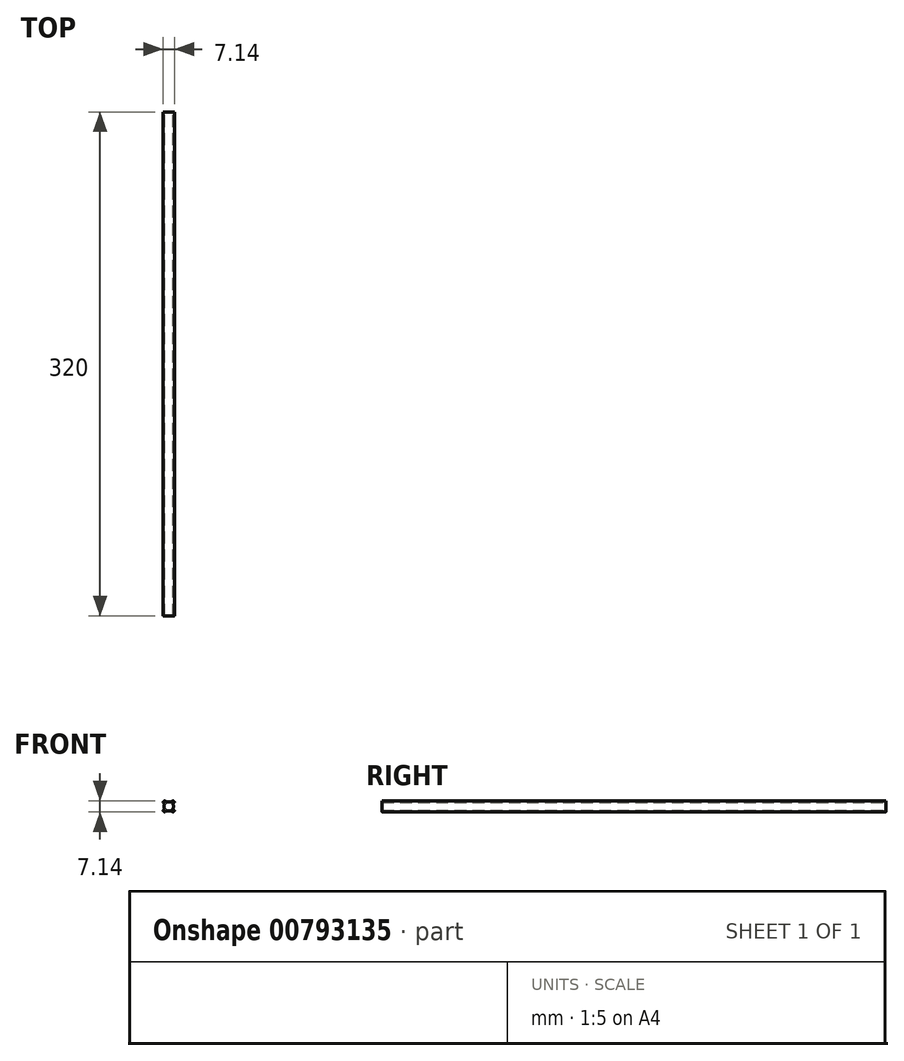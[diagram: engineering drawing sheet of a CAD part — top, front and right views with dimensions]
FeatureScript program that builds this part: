
annotation { "Feature Type Name" : "Feature", "Feature Type Description" : "" }
export const myFeature = defineFeature(function(context is Context, id is Id, definition is map)
    precondition{}
    {
        {
            var Q0;
            Q0=qCreatedBy(makeId("Front.planeOp"),FACE);
            var sketch = newSketch(context, id + "F0", { "sketchPlane" : qUnion([Q0])});
            skArc(sketch, "E0", {"start": v(-18.98, 50.3) * mm, "mid": v(-19, 50.49) * mm, "end": v(-18.92, 50.65) * mm});
            skLineSegment(sketch, "E1", {"start": v(-18.92, 50.65) * mm, "end": v(-18.18, 51.4) * mm});
            skArc(sketch, "E2", {"start": v(-18.18, 51.4) * mm, "mid": v(-18.1, 51.59) * mm, "end": v(-18.16, 51.8) * mm});
            skArc(sketch, "E3", {"start": v(-18.16, 51.8) * mm, "mid": v(-18.49, 52.15) * mm, "end": v(-18.84, 52.47) * mm});
            skArc(sketch, "E4", {"start": v(-18.84, 52.47) * mm, "mid": v(-19.05, 52.54) * mm, "end": v(-19.25, 52.45) * mm});
            skLineSegment(sketch, "E5", {"start": v(-19.25, 52.45) * mm, "end": v(-19.99, 51.71) * mm});
            skArc(sketch, "E6", {"start": v(-19.99, 51.71) * mm, "mid": v(-20.15, 51.63) * mm, "end": v(-20.33, 51.65) * mm});
            skArc(sketch, "E7", {"start": v(-20.33, 51.65) * mm, "mid": v(-21.67, 51.97) * mm, "end": v(-23, 51.65) * mm});
            skArc(sketch, "E8", {"start": v(-23, 51.65) * mm, "mid": v(-23.19, 51.63) * mm, "end": v(-23.35, 51.7) * mm});
            skLineSegment(sketch, "E9", {"start": v(-23.35, 51.7) * mm, "end": v(-24.1, 52.45) * mm});
            skArc(sketch, "E10", {"start": v(-24.1, 52.45) * mm, "mid": v(-24.29, 52.54) * mm, "end": v(-24.5, 52.47) * mm});
            skArc(sketch, "E11", {"start": v(-24.5, 52.47) * mm, "mid": v(-24.85, 52.15) * mm, "end": v(-25.17, 51.79) * mm});
            skArc(sketch, "E12", {"start": v(-25.17, 51.79) * mm, "mid": v(-25.24, 51.59) * mm, "end": v(-25.15, 51.39) * mm});
            skLineSegment(sketch, "E13", {"start": v(-25.15, 51.39) * mm, "end": v(-24.4, 50.65) * mm});
            skArc(sketch, "E14", {"start": v(-24.4, 50.65) * mm, "mid": v(-24.33, 50.49) * mm, "end": v(-24.35, 50.3) * mm});
            skArc(sketch, "E15", {"start": v(-24.35, 50.3) * mm, "mid": v(-24.67, 48.97) * mm, "end": v(-24.35, 47.63) * mm});
            skArc(sketch, "E16", {"start": v(-24.35, 47.63) * mm, "mid": v(-24.33, 47.45) * mm, "end": v(-24.4, 47.29) * mm});
            skLineSegment(sketch, "E17", {"start": v(-24.4, 47.29) * mm, "end": v(-25.15, 46.54) * mm});
            skArc(sketch, "E18", {"start": v(-25.15, 46.54) * mm, "mid": v(-25.24, 46.35) * mm, "end": v(-25.17, 46.14) * mm});
            skArc(sketch, "E19", {"start": v(-25.17, 46.14) * mm, "mid": v(-24.85, 45.79) * mm, "end": v(-24.49, 45.46) * mm});
            skArc(sketch, "E20", {"start": v(-24.49, 45.46) * mm, "mid": v(-24.29, 45.4) * mm, "end": v(-24.09, 45.48) * mm});
            skLineSegment(sketch, "E21", {"start": v(-24.09, 45.48) * mm, "end": v(-23.35, 46.22) * mm});
            skArc(sketch, "E22", {"start": v(-23.35, 46.22) * mm, "mid": v(-23.19, 46.3) * mm, "end": v(-23, 46.28) * mm});
            skArc(sketch, "E23", {"start": v(-23, 46.28) * mm, "mid": v(-21.67, 45.97) * mm, "end": v(-20.33, 46.28) * mm});
            skArc(sketch, "E24", {"start": v(-20.33, 46.28) * mm, "mid": v(-20.15, 46.3) * mm, "end": v(-19.99, 46.23) * mm});
            skLineSegment(sketch, "E25", {"start": v(-19.99, 46.23) * mm, "end": v(-19.24, 45.48) * mm});
            skArc(sketch, "E26", {"start": v(-19.24, 45.48) * mm, "mid": v(-19.05, 45.4) * mm, "end": v(-18.84, 45.46) * mm});
            skArc(sketch, "E27", {"start": v(-18.84, 45.46) * mm, "mid": v(-18.49, 45.79) * mm, "end": v(-18.16, 46.14) * mm});
            skArc(sketch, "E28", {"start": v(-18.16, 46.14) * mm, "mid": v(-18.1, 46.35) * mm, "end": v(-18.18, 46.55) * mm});
            skLineSegment(sketch, "E29", {"start": v(-18.18, 46.55) * mm, "end": v(-18.92, 47.29) * mm});
            skArc(sketch, "E30", {"start": v(-18.92, 47.29) * mm, "mid": v(-19, 47.45) * mm, "end": v(-18.98, 47.63) * mm});
            skArc(sketch, "E31", {"start": v(-18.98, 47.63) * mm, "mid": v(-18.67, 48.97) * mm, "end": v(-18.98, 50.3) * mm});
            skLineSegment(sketch, "E32", {"start": v(-21.67, 51.17) * mm, "end": v(-21.67, 46.77) * mm});
            skLineSegment(sketch, "E33", {"start": v(-19.47, 48.97) * mm, "end": v(-23.87, 48.97) * mm});
            skLineSegment(sketch, "E34", {"start": v(-19.47, 68.97) * mm, "end": v(-23.87, 68.97) * mm});
            skLineSegment(sketch, "E35", {"start": v(-21.67, 66.77) * mm, "end": v(-21.67, 71.17) * mm});
            skArc(sketch, "E36", {"start": v(-8.43, 60.55) * mm, "mid": v(-8.21, 60.72) * mm, "end": v(-8.23, 61) * mm});
            skArc(sketch, "E37", {"start": v(-8.23, 61) * mm, "mid": v(-8.84, 61.8) * mm, "end": v(-9.63, 62.41) * mm});
            skArc(sketch, "E38", {"start": v(-9.63, 62.41) * mm, "mid": v(-9.91, 62.43) * mm, "end": v(-10.08, 62.2) * mm});
            skLineSegment(sketch, "E39", {"start": v(-10.08, 62.2) * mm, "end": v(-10.22, 61.46) * mm});
            skArc(sketch, "E40", {"start": v(-10.22, 61.46) * mm, "mid": v(-10.37, 61.25) * mm, "end": v(-10.63, 61.24) * mm});
            skArc(sketch, "E41", {"start": v(-10.63, 61.24) * mm, "mid": v(-11.67, 61.47) * mm, "end": v(-12.7, 61.24) * mm});
            skArc(sketch, "E42", {"start": v(-12.7, 61.24) * mm, "mid": v(-12.96, 61.25) * mm, "end": v(-13.12, 61.46) * mm});
            skLineSegment(sketch, "E43", {"start": v(-13.12, 61.46) * mm, "end": v(-13.25, 62.2) * mm});
            skArc(sketch, "E44", {"start": v(-13.25, 62.2) * mm, "mid": v(-13.42, 62.43) * mm, "end": v(-13.7, 62.41) * mm});
            skArc(sketch, "E45", {"start": v(-13.7, 62.41) * mm, "mid": v(-14.5, 61.8) * mm, "end": v(-15.11, 61) * mm});
            skArc(sketch, "E46", {"start": v(-15.11, 61) * mm, "mid": v(-15.12, 60.72) * mm, "end": v(-14.9, 60.55) * mm});
            skLineSegment(sketch, "E47", {"start": v(-14.9, 60.55) * mm, "end": v(-14.16, 60.42) * mm});
            skArc(sketch, "E48", {"start": v(-14.16, 60.42) * mm, "mid": v(-13.95, 60.26) * mm, "end": v(-13.94, 60) * mm});
            skArc(sketch, "E49", {"start": v(-13.94, 60) * mm, "mid": v(-14.17, 58.97) * mm, "end": v(-13.94, 57.93) * mm});
            skArc(sketch, "E50", {"start": v(-13.94, 57.93) * mm, "mid": v(-13.95, 57.67) * mm, "end": v(-14.16, 57.52) * mm});
            skLineSegment(sketch, "E51", {"start": v(-14.16, 57.52) * mm, "end": v(-14.9, 57.38) * mm});
            skArc(sketch, "E52", {"start": v(-14.9, 57.38) * mm, "mid": v(-15.12, 57.21) * mm, "end": v(-15.11, 56.93) * mm});
            skArc(sketch, "E53", {"start": v(-15.11, 56.93) * mm, "mid": v(-14.5, 56.14) * mm, "end": v(-13.7, 55.53) * mm});
            skArc(sketch, "E54", {"start": v(-13.7, 55.53) * mm, "mid": v(-13.42, 55.51) * mm, "end": v(-13.25, 55.73) * mm});
            skLineSegment(sketch, "E55", {"start": v(-13.25, 55.73) * mm, "end": v(-13.12, 56.47) * mm});
            skArc(sketch, "E56", {"start": v(-13.12, 56.47) * mm, "mid": v(-12.96, 56.68) * mm, "end": v(-12.7, 56.7) * mm});
            skArc(sketch, "E57", {"start": v(-12.7, 56.7) * mm, "mid": v(-11.67, 56.47) * mm, "end": v(-10.63, 56.7) * mm});
            skArc(sketch, "E58", {"start": v(-10.63, 56.7) * mm, "mid": v(-10.37, 56.68) * mm, "end": v(-10.22, 56.47) * mm});
            skLineSegment(sketch, "E59", {"start": v(-10.22, 56.47) * mm, "end": v(-10.08, 55.73) * mm});
            skArc(sketch, "E60", {"start": v(-10.08, 55.73) * mm, "mid": v(-9.91, 55.51) * mm, "end": v(-9.63, 55.53) * mm});
            skArc(sketch, "E61", {"start": v(-9.63, 55.53) * mm, "mid": v(-8.84, 56.14) * mm, "end": v(-8.23, 56.93) * mm});
            skArc(sketch, "E62", {"start": v(-8.23, 56.93) * mm, "mid": v(-8.21, 57.21) * mm, "end": v(-8.43, 57.38) * mm});
            skLineSegment(sketch, "E63", {"start": v(-8.43, 57.38) * mm, "end": v(-9.17, 57.52) * mm});
            skArc(sketch, "E64", {"start": v(-9.17, 57.52) * mm, "mid": v(-9.38, 57.67) * mm, "end": v(-9.4, 57.93) * mm});
            skArc(sketch, "E65", {"start": v(-9.4, 57.93) * mm, "mid": v(-9.17, 58.97) * mm, "end": v(-9.4, 60) * mm});
            skArc(sketch, "E66", {"start": v(-9.4, 60) * mm, "mid": v(-9.38, 60.26) * mm, "end": v(-9.17, 60.42) * mm});
            skLineSegment(sketch, "E67", {"start": v(-9.17, 60.42) * mm, "end": v(-8.43, 60.55) * mm});
            skArc(sketch, "E68", {"start": v(-18.98, 67.63) * mm, "mid": v(-19, 67.45) * mm, "end": v(-18.93, 67.29) * mm});
            skLineSegment(sketch, "E69", {"start": v(-18.93, 67.29) * mm, "end": v(-18.19, 66.55) * mm});
            skArc(sketch, "E70", {"start": v(-18.19, 66.55) * mm, "mid": v(-18.1, 66.35) * mm, "end": v(-18.16, 66.15) * mm});
            skArc(sketch, "E71", {"start": v(-18.16, 66.15) * mm, "mid": v(-18.49, 65.79) * mm, "end": v(-18.85, 65.46) * mm});
            skArc(sketch, "E72", {"start": v(-18.85, 65.46) * mm, "mid": v(-19.05, 65.4) * mm, "end": v(-19.25, 65.49) * mm});
            skLineSegment(sketch, "E73", {"start": v(-19.25, 65.49) * mm, "end": v(-19.99, 66.23) * mm});
            skArc(sketch, "E74", {"start": v(-19.99, 66.23) * mm, "mid": v(-20.15, 66.3) * mm, "end": v(-20.33, 66.28) * mm});
            skArc(sketch, "E75", {"start": v(-20.33, 66.28) * mm, "mid": v(-21.67, 65.97) * mm, "end": v(-23, 66.28) * mm});
            skArc(sketch, "E76", {"start": v(-23, 66.28) * mm, "mid": v(-23.19, 66.3) * mm, "end": v(-23.35, 66.23) * mm});
            skLineSegment(sketch, "E77", {"start": v(-23.35, 66.23) * mm, "end": v(-24.1, 65.49) * mm});
            skArc(sketch, "E78", {"start": v(-24.1, 65.49) * mm, "mid": v(-24.29, 65.4) * mm, "end": v(-24.5, 65.46) * mm});
            skArc(sketch, "E79", {"start": v(-24.5, 65.46) * mm, "mid": v(-24.85, 65.79) * mm, "end": v(-25.17, 66.15) * mm});
            skArc(sketch, "E80", {"start": v(-25.17, 66.15) * mm, "mid": v(-25.24, 66.35) * mm, "end": v(-25.15, 66.55) * mm});
            skLineSegment(sketch, "E81", {"start": v(-25.15, 66.55) * mm, "end": v(-24.41, 67.29) * mm});
            skArc(sketch, "E82", {"start": v(-24.41, 67.29) * mm, "mid": v(-24.33, 67.45) * mm, "end": v(-24.35, 67.63) * mm});
            skArc(sketch, "E83", {"start": v(-24.35, 67.63) * mm, "mid": v(-24.67, 68.97) * mm, "end": v(-24.35, 70.3) * mm});
            skArc(sketch, "E84", {"start": v(-24.35, 70.3) * mm, "mid": v(-24.33, 70.49) * mm, "end": v(-24.41, 70.65) * mm});
            skLineSegment(sketch, "E85", {"start": v(-24.41, 70.65) * mm, "end": v(-25.15, 71.4) * mm});
            skArc(sketch, "E86", {"start": v(-25.15, 71.4) * mm, "mid": v(-25.24, 71.59) * mm, "end": v(-25.17, 71.8) * mm});
            skArc(sketch, "E87", {"start": v(-25.17, 71.8) * mm, "mid": v(-24.85, 72.15) * mm, "end": v(-24.5, 72.47) * mm});
            skArc(sketch, "E88", {"start": v(-24.5, 72.47) * mm, "mid": v(-24.29, 72.54) * mm, "end": v(-24.1, 72.45) * mm});
            skLineSegment(sketch, "E89", {"start": v(-24.1, 72.45) * mm, "end": v(-23.35, 71.71) * mm});
            skArc(sketch, "E90", {"start": v(-23.35, 71.71) * mm, "mid": v(-23.19, 71.63) * mm, "end": v(-23, 71.65) * mm});
            skArc(sketch, "E91", {"start": v(-23, 71.65) * mm, "mid": v(-21.67, 71.97) * mm, "end": v(-20.33, 71.65) * mm});
            skArc(sketch, "E92", {"start": v(-20.33, 71.65) * mm, "mid": v(-20.15, 71.63) * mm, "end": v(-19.99, 71.71) * mm});
            skLineSegment(sketch, "E93", {"start": v(-19.99, 71.71) * mm, "end": v(-19.25, 72.45) * mm});
            skArc(sketch, "E94", {"start": v(-19.25, 72.45) * mm, "mid": v(-19.05, 72.54) * mm, "end": v(-18.85, 72.47) * mm});
            skArc(sketch, "E95", {"start": v(-18.85, 72.47) * mm, "mid": v(-18.49, 72.15) * mm, "end": v(-18.16, 71.8) * mm});
            skArc(sketch, "E96", {"start": v(-18.16, 71.8) * mm, "mid": v(-18.1, 71.59) * mm, "end": v(-18.19, 71.4) * mm});
            skLineSegment(sketch, "E97", {"start": v(-18.19, 71.4) * mm, "end": v(-18.93, 70.65) * mm});
            skArc(sketch, "E98", {"start": v(-18.93, 70.65) * mm, "mid": v(-19, 70.49) * mm, "end": v(-18.98, 70.3) * mm});
            skArc(sketch, "E99", {"start": v(-18.98, 70.3) * mm, "mid": v(-18.67, 68.97) * mm, "end": v(-18.98, 67.63) * mm});
            skLineSegment(sketch, "E100", {"start": v(-6.66, 58.97) * mm, "end": v(-6.16, 58.97) * mm});
            skArc(sketch, "E101", {"start": v(21.57, 60.55) * mm, "mid": v(21.79, 60.72) * mm, "end": v(21.77, 61) * mm});
            skArc(sketch, "E102", {"start": v(21.77, 61) * mm, "mid": v(21.16, 61.8) * mm, "end": v(20.37, 62.41) * mm});
            skArc(sketch, "E103", {"start": v(20.37, 62.41) * mm, "mid": v(20.09, 62.43) * mm, "end": v(19.92, 62.2) * mm});
            skLineSegment(sketch, "E104", {"start": v(19.92, 62.2) * mm, "end": v(19.78, 61.46) * mm});
            skArc(sketch, "E105", {"start": v(19.78, 61.46) * mm, "mid": v(19.63, 61.25) * mm, "end": v(19.37, 61.24) * mm});
            skArc(sketch, "E106", {"start": v(19.37, 61.24) * mm, "mid": v(18.33, 61.47) * mm, "end": v(17.3, 61.24) * mm});
            skArc(sketch, "E107", {"start": v(17.3, 61.24) * mm, "mid": v(17.04, 61.25) * mm, "end": v(16.88, 61.46) * mm});
            skLineSegment(sketch, "E108", {"start": v(16.88, 61.46) * mm, "end": v(16.75, 62.2) * mm});
            skArc(sketch, "E109", {"start": v(16.75, 62.2) * mm, "mid": v(16.58, 62.43) * mm, "end": v(16.3, 62.41) * mm});
            skArc(sketch, "E110", {"start": v(16.3, 62.41) * mm, "mid": v(15.5, 61.8) * mm, "end": v(14.89, 61) * mm});
            skArc(sketch, "E111", {"start": v(14.89, 61) * mm, "mid": v(14.88, 60.72) * mm, "end": v(15.1, 60.55) * mm});
            skLineSegment(sketch, "E112", {"start": v(15.1, 60.55) * mm, "end": v(15.84, 60.42) * mm});
            skArc(sketch, "E113", {"start": v(15.84, 60.42) * mm, "mid": v(16.05, 60.26) * mm, "end": v(16.06, 60) * mm});
            skArc(sketch, "E114", {"start": v(16.06, 60) * mm, "mid": v(15.83, 58.97) * mm, "end": v(16.06, 57.93) * mm});
            skArc(sketch, "E115", {"start": v(16.06, 57.93) * mm, "mid": v(16.05, 57.67) * mm, "end": v(15.84, 57.52) * mm});
            skLineSegment(sketch, "E116", {"start": v(15.84, 57.52) * mm, "end": v(15.1, 57.38) * mm});
            skArc(sketch, "E117", {"start": v(15.1, 57.38) * mm, "mid": v(14.88, 57.21) * mm, "end": v(14.89, 56.93) * mm});
            skArc(sketch, "E118", {"start": v(14.89, 56.93) * mm, "mid": v(15.5, 56.14) * mm, "end": v(16.3, 55.53) * mm});
            skArc(sketch, "E119", {"start": v(16.3, 55.53) * mm, "mid": v(16.58, 55.51) * mm, "end": v(16.75, 55.73) * mm});
            skLineSegment(sketch, "E120", {"start": v(16.75, 55.73) * mm, "end": v(16.88, 56.47) * mm});
            skArc(sketch, "E121", {"start": v(16.88, 56.47) * mm, "mid": v(17.04, 56.68) * mm, "end": v(17.3, 56.7) * mm});
            skArc(sketch, "E122", {"start": v(17.3, 56.7) * mm, "mid": v(18.33, 56.47) * mm, "end": v(19.37, 56.7) * mm});
            skArc(sketch, "E123", {"start": v(19.37, 56.7) * mm, "mid": v(19.63, 56.68) * mm, "end": v(19.78, 56.47) * mm});
            skLineSegment(sketch, "E124", {"start": v(19.78, 56.47) * mm, "end": v(19.92, 55.73) * mm});
            skArc(sketch, "E125", {"start": v(19.92, 55.73) * mm, "mid": v(20.09, 55.51) * mm, "end": v(20.37, 55.53) * mm});
            skArc(sketch, "E126", {"start": v(20.37, 55.53) * mm, "mid": v(21.16, 56.14) * mm, "end": v(21.77, 56.93) * mm});
            skArc(sketch, "E127", {"start": v(21.77, 56.93) * mm, "mid": v(21.79, 57.21) * mm, "end": v(21.57, 57.38) * mm});
            skLineSegment(sketch, "E128", {"start": v(21.57, 57.38) * mm, "end": v(20.83, 57.52) * mm});
            skArc(sketch, "E129", {"start": v(20.83, 57.52) * mm, "mid": v(20.62, 57.67) * mm, "end": v(20.6, 57.93) * mm});
            skArc(sketch, "E130", {"start": v(20.6, 57.93) * mm, "mid": v(20.83, 58.97) * mm, "end": v(20.6, 60) * mm});
            skArc(sketch, "E131", {"start": v(20.6, 60) * mm, "mid": v(20.62, 60.26) * mm, "end": v(20.83, 60.42) * mm});
            skLineSegment(sketch, "E132", {"start": v(20.83, 60.42) * mm, "end": v(21.57, 60.55) * mm});
            skArc(sketch, "E133", {"start": v(25.64, 50.3) * mm, "mid": v(25.67, 50.49) * mm, "end": v(25.59, 50.65) * mm});
            skLineSegment(sketch, "E134", {"start": v(25.59, 50.65) * mm, "end": v(24.85, 51.4) * mm});
            skArc(sketch, "E135", {"start": v(24.85, 51.4) * mm, "mid": v(24.76, 51.59) * mm, "end": v(24.82, 51.8) * mm});
            skArc(sketch, "E136", {"start": v(24.82, 51.8) * mm, "mid": v(25.15, 52.15) * mm, "end": v(25.5, 52.47) * mm});
            skArc(sketch, "E137", {"start": v(25.5, 52.47) * mm, "mid": v(25.71, 52.54) * mm, "end": v(25.9, 52.45) * mm});
            skLineSegment(sketch, "E138", {"start": v(25.9, 52.45) * mm, "end": v(26.65, 51.71) * mm});
            skArc(sketch, "E139", {"start": v(26.65, 51.71) * mm, "mid": v(26.81, 51.63) * mm, "end": v(27, 51.65) * mm});
            skArc(sketch, "E140", {"start": v(27, 51.65) * mm, "mid": v(28.33, 51.97) * mm, "end": v(29.67, 51.65) * mm});
            skArc(sketch, "E141", {"start": v(29.67, 51.65) * mm, "mid": v(29.85, 51.63) * mm, "end": v(30.01, 51.7) * mm});
            skLineSegment(sketch, "E142", {"start": v(30.01, 51.7) * mm, "end": v(30.75, 52.45) * mm});
            skArc(sketch, "E143", {"start": v(30.75, 52.45) * mm, "mid": v(30.95, 52.54) * mm, "end": v(31.15, 52.47) * mm});
            skArc(sketch, "E144", {"start": v(31.15, 52.47) * mm, "mid": v(31.51, 52.15) * mm, "end": v(31.83, 51.79) * mm});
            skArc(sketch, "E145", {"start": v(31.83, 51.79) * mm, "mid": v(31.9, 51.59) * mm, "end": v(31.81, 51.39) * mm});
            skLineSegment(sketch, "E146", {"start": v(31.81, 51.39) * mm, "end": v(31.07, 50.65) * mm});
            skArc(sketch, "E147", {"start": v(31.07, 50.65) * mm, "mid": v(30.99, 50.49) * mm, "end": v(31.01, 50.3) * mm});
            skArc(sketch, "E148", {"start": v(31.01, 50.3) * mm, "mid": v(31.33, 48.97) * mm, "end": v(31.01, 47.63) * mm});
            skArc(sketch, "E149", {"start": v(31.01, 47.63) * mm, "mid": v(30.99, 47.45) * mm, "end": v(31.07, 47.29) * mm});
            skLineSegment(sketch, "E150", {"start": v(31.07, 47.29) * mm, "end": v(31.81, 46.54) * mm});
            skArc(sketch, "E151", {"start": v(31.81, 46.54) * mm, "mid": v(31.9, 46.35) * mm, "end": v(31.83, 46.14) * mm});
            skArc(sketch, "E152", {"start": v(31.83, 46.14) * mm, "mid": v(31.51, 45.79) * mm, "end": v(31.15, 45.46) * mm});
            skArc(sketch, "E153", {"start": v(31.15, 45.46) * mm, "mid": v(30.95, 45.4) * mm, "end": v(30.75, 45.48) * mm});
            skLineSegment(sketch, "E154", {"start": v(30.75, 45.48) * mm, "end": v(30.01, 46.22) * mm});
            skArc(sketch, "E155", {"start": v(30.01, 46.22) * mm, "mid": v(29.85, 46.3) * mm, "end": v(29.66, 46.28) * mm});
            skArc(sketch, "E156", {"start": v(29.66, 46.28) * mm, "mid": v(28.33, 45.97) * mm, "end": v(27, 46.28) * mm});
            skArc(sketch, "E157", {"start": v(27, 46.28) * mm, "mid": v(26.81, 46.3) * mm, "end": v(26.65, 46.23) * mm});
            skLineSegment(sketch, "E158", {"start": v(26.65, 46.23) * mm, "end": v(25.9, 45.48) * mm});
            skArc(sketch, "E159", {"start": v(25.9, 45.48) * mm, "mid": v(25.71, 45.4) * mm, "end": v(25.5, 45.46) * mm});
            skArc(sketch, "E160", {"start": v(25.5, 45.46) * mm, "mid": v(25.15, 45.79) * mm, "end": v(24.82, 46.14) * mm});
            skArc(sketch, "E161", {"start": v(24.82, 46.14) * mm, "mid": v(24.76, 46.35) * mm, "end": v(24.85, 46.55) * mm});
            skLineSegment(sketch, "E162", {"start": v(24.85, 46.55) * mm, "end": v(25.59, 47.29) * mm});
            skArc(sketch, "E163", {"start": v(25.59, 47.29) * mm, "mid": v(25.67, 47.45) * mm, "end": v(25.64, 47.63) * mm});
            skArc(sketch, "E164", {"start": v(25.64, 47.63) * mm, "mid": v(25.33, 48.97) * mm, "end": v(25.64, 50.3) * mm});
            skLineSegment(sketch, "E165", {"start": v(28.33, 51.17) * mm, "end": v(28.33, 46.77) * mm});
            skLineSegment(sketch, "E166", {"start": v(26.13, 48.97) * mm, "end": v(30.53, 48.97) * mm});
            skArc(sketch, "E167", {"start": v(25.64, 67.63) * mm, "mid": v(25.67, 67.45) * mm, "end": v(25.59, 67.29) * mm});
            skLineSegment(sketch, "E168", {"start": v(25.59, 67.29) * mm, "end": v(24.85, 66.55) * mm});
            skArc(sketch, "E169", {"start": v(24.85, 66.55) * mm, "mid": v(24.76, 66.35) * mm, "end": v(24.82, 66.15) * mm});
            skArc(sketch, "E170", {"start": v(24.82, 66.15) * mm, "mid": v(25.15, 65.79) * mm, "end": v(25.5, 65.46) * mm});
            skArc(sketch, "E171", {"start": v(25.5, 65.46) * mm, "mid": v(25.71, 65.4) * mm, "end": v(25.9, 65.49) * mm});
            skLineSegment(sketch, "E172", {"start": v(25.9, 65.49) * mm, "end": v(26.65, 66.23) * mm});
            skArc(sketch, "E173", {"start": v(26.65, 66.23) * mm, "mid": v(26.81, 66.3) * mm, "end": v(27, 66.28) * mm});
            skArc(sketch, "E174", {"start": v(27, 66.28) * mm, "mid": v(28.33, 65.97) * mm, "end": v(29.67, 66.28) * mm});
            skArc(sketch, "E175", {"start": v(29.67, 66.28) * mm, "mid": v(29.85, 66.3) * mm, "end": v(30.01, 66.23) * mm});
            skLineSegment(sketch, "E176", {"start": v(30.01, 66.23) * mm, "end": v(30.75, 65.49) * mm});
            skArc(sketch, "E177", {"start": v(30.75, 65.49) * mm, "mid": v(30.95, 65.4) * mm, "end": v(31.15, 65.46) * mm});
            skArc(sketch, "E178", {"start": v(31.15, 65.46) * mm, "mid": v(31.51, 65.79) * mm, "end": v(31.83, 66.15) * mm});
            skArc(sketch, "E179", {"start": v(31.83, 66.15) * mm, "mid": v(31.9, 66.35) * mm, "end": v(31.81, 66.55) * mm});
            skLineSegment(sketch, "E180", {"start": v(31.81, 66.55) * mm, "end": v(31.07, 67.29) * mm});
            skArc(sketch, "E181", {"start": v(31.07, 67.29) * mm, "mid": v(30.99, 67.45) * mm, "end": v(31.02, 67.63) * mm});
            skArc(sketch, "E182", {"start": v(31.02, 67.63) * mm, "mid": v(31.33, 68.97) * mm, "end": v(31.02, 70.3) * mm});
            skArc(sketch, "E183", {"start": v(31.02, 70.3) * mm, "mid": v(30.99, 70.49) * mm, "end": v(31.07, 70.65) * mm});
            skLineSegment(sketch, "E184", {"start": v(31.07, 70.65) * mm, "end": v(31.81, 71.4) * mm});
            skArc(sketch, "E185", {"start": v(31.81, 71.4) * mm, "mid": v(31.9, 71.59) * mm, "end": v(31.83, 71.8) * mm});
            skArc(sketch, "E186", {"start": v(31.83, 71.8) * mm, "mid": v(31.51, 72.15) * mm, "end": v(31.15, 72.47) * mm});
            skArc(sketch, "E187", {"start": v(31.15, 72.47) * mm, "mid": v(30.95, 72.54) * mm, "end": v(30.75, 72.45) * mm});
            skLineSegment(sketch, "E188", {"start": v(30.75, 72.45) * mm, "end": v(30.01, 71.71) * mm});
            skArc(sketch, "E189", {"start": v(30.01, 71.71) * mm, "mid": v(29.85, 71.63) * mm, "end": v(29.67, 71.65) * mm});
            skArc(sketch, "E190", {"start": v(29.67, 71.65) * mm, "mid": v(28.33, 71.97) * mm, "end": v(27, 71.65) * mm});
            skArc(sketch, "E191", {"start": v(27, 71.65) * mm, "mid": v(26.81, 71.63) * mm, "end": v(26.65, 71.71) * mm});
            skLineSegment(sketch, "E192", {"start": v(26.65, 71.71) * mm, "end": v(25.9, 72.45) * mm});
            skArc(sketch, "E193", {"start": v(25.9, 72.45) * mm, "mid": v(25.71, 72.54) * mm, "end": v(25.5, 72.47) * mm});
            skArc(sketch, "E194", {"start": v(25.5, 72.47) * mm, "mid": v(25.15, 72.15) * mm, "end": v(24.82, 71.8) * mm});
            skArc(sketch, "E195", {"start": v(24.82, 71.8) * mm, "mid": v(24.76, 71.59) * mm, "end": v(24.85, 71.4) * mm});
            skLineSegment(sketch, "E196", {"start": v(24.85, 71.4) * mm, "end": v(25.59, 70.65) * mm});
            skArc(sketch, "E197", {"start": v(25.59, 70.65) * mm, "mid": v(25.67, 70.49) * mm, "end": v(25.64, 70.3) * mm});
            skArc(sketch, "E198", {"start": v(25.64, 70.3) * mm, "mid": v(25.33, 68.97) * mm, "end": v(25.64, 67.63) * mm});
            skLineSegment(sketch, "E199", {"start": v(26.13, 68.97) * mm, "end": v(30.53, 68.97) * mm});
            skLineSegment(sketch, "E200", {"start": v(28.33, 66.77) * mm, "end": v(28.33, 71.17) * mm});
            skLineSegment(sketch, "E201", {"start": v(13.33, 58.97) * mm, "end": v(12.83, 58.97) * mm});
            skLineSegment(sketch, "E202", {"start": v(11.4, 65.24) * mm, "end": v(13.2, 63.32) * mm});
            skArc(sketch, "E203", {"start": v(13.2, 63.32) * mm, "mid": v(13.3, 63.17) * mm, "end": v(13.33, 62.98) * mm});
            skLineSegment(sketch, "E204", {"start": v(13.33, 62.98) * mm, "end": v(13.33, 59.47) * mm});
            skLineSegment(sketch, "E205", {"start": v(13.33, 59.47) * mm, "end": v(13.83, 58.97) * mm});
            skLineSegment(sketch, "E206", {"start": v(13.83, 58.97) * mm, "end": v(13.33, 58.47) * mm});
            skLineSegment(sketch, "E207", {"start": v(13.33, 58.47) * mm, "end": v(13.33, 54.95) * mm});
            skArc(sketch, "E208", {"start": v(13.33, 54.95) * mm, "mid": v(13.3, 54.77) * mm, "end": v(13.2, 54.61) * mm});
            skLineSegment(sketch, "E209", {"start": v(13.2, 54.61) * mm, "end": v(11.4, 52.7) * mm});
            skArc(sketch, "E210", {"start": v(11.4, 52.7) * mm, "mid": v(10.42, 50.82) * mm, "end": v(10.53, 48.71) * mm});
            skLineSegment(sketch, "E211", {"start": v(10.53, 48.71) * mm, "end": v(11.48, 46.68) * mm});
            skArc(sketch, "E212", {"start": v(11.48, 46.68) * mm, "mid": v(11.45, 46.2) * mm, "end": v(11.03, 45.97) * mm});
            skLineSegment(sketch, "E213", {"start": v(11.03, 45.97) * mm, "end": v(-4.36, 45.97) * mm});
            skArc(sketch, "E214", {"start": v(-4.36, 45.97) * mm, "mid": v(-4.78, 46.2) * mm, "end": v(-4.81, 46.68) * mm});
            skLineSegment(sketch, "E215", {"start": v(-4.81, 46.68) * mm, "end": v(-3.87, 48.71) * mm});
            skArc(sketch, "E216", {"start": v(-3.87, 48.71) * mm, "mid": v(-3.76, 50.82) * mm, "end": v(-4.75, 52.7) * mm});
            skLineSegment(sketch, "E217", {"start": v(-4.75, 52.7) * mm, "end": v(-6.53, 54.61) * mm});
            skArc(sketch, "E218", {"start": v(-6.53, 54.61) * mm, "mid": v(-6.63, 54.77) * mm, "end": v(-6.67, 54.95) * mm});
            skLineSegment(sketch, "E219", {"start": v(-6.67, 54.95) * mm, "end": v(-6.67, 58.47) * mm});
            skLineSegment(sketch, "E220", {"start": v(-6.67, 58.47) * mm, "end": v(-7.17, 58.97) * mm});
            skLineSegment(sketch, "E221", {"start": v(-7.17, 58.97) * mm, "end": v(-6.67, 59.47) * mm});
            skLineSegment(sketch, "E222", {"start": v(-6.67, 59.47) * mm, "end": v(-6.67, 62.98) * mm});
            skArc(sketch, "E223", {"start": v(-6.67, 62.98) * mm, "mid": v(-6.63, 63.17) * mm, "end": v(-6.53, 63.32) * mm});
            skLineSegment(sketch, "E224", {"start": v(-6.53, 63.32) * mm, "end": v(-4.75, 65.24) * mm});
            skArc(sketch, "E225", {"start": v(-4.75, 65.24) * mm, "mid": v(-3.76, 67.11) * mm, "end": v(-3.87, 69.23) * mm});
            skLineSegment(sketch, "E226", {"start": v(-3.87, 69.23) * mm, "end": v(-4.81, 71.26) * mm});
            skArc(sketch, "E227", {"start": v(-4.81, 71.26) * mm, "mid": v(-4.78, 71.74) * mm, "end": v(-4.36, 71.97) * mm});
            skLineSegment(sketch, "E228", {"start": v(-4.36, 71.97) * mm, "end": v(11.03, 71.97) * mm});
            skArc(sketch, "E229", {"start": v(11.03, 71.97) * mm, "mid": v(11.45, 71.74) * mm, "end": v(11.48, 71.26) * mm});
            skLineSegment(sketch, "E230", {"start": v(11.48, 71.26) * mm, "end": v(10.53, 69.23) * mm});
            skArc(sketch, "E231", {"start": v(10.53, 69.23) * mm, "mid": v(10.42, 67.11) * mm, "end": v(11.4, 65.24) * mm});
            skLineSegment(sketch, "E232", {"start": v(-7.72, 43.97) * mm, "end": v(14.38, 43.97) * mm});
            skLineSegment(sketch, "E233", {"start": v(14.38, 43.97) * mm, "end": v(15.18, 44.47) * mm});
            skLineSegment(sketch, "E234", {"start": v(15.18, 44.47) * mm, "end": v(15.18, 46.17) * mm});
            skArc(sketch, "E235", {"start": v(15.18, 46.17) * mm, "mid": v(15.1, 46.38) * mm, "end": v(14.88, 46.47) * mm});
            skLineSegment(sketch, "E236", {"start": v(14.88, 46.47) * mm, "end": v(13.23, 46.47) * mm});
            skLineSegment(sketch, "E237", {"start": v(13.23, 46.47) * mm, "end": v(12.24, 49.52) * mm});
            skArc(sketch, "E238", {"start": v(12.24, 49.52) * mm, "mid": v(12.2, 49.78) * mm, "end": v(12.22, 50.04) * mm});
            skArc(sketch, "E239", {"start": v(12.22, 50.04) * mm, "mid": v(13.06, 52.08) * mm, "end": v(14.33, 53.88) * mm});
            skArc(sketch, "E240", {"start": v(14.33, 53.88) * mm, "mid": v(15.17, 54.32) * mm, "end": v(16.11, 54.47) * mm});
            skLineSegment(sketch, "E241", {"start": v(16.11, 54.47) * mm, "end": v(17.83, 54.47) * mm});
            skLineSegment(sketch, "E242", {"start": v(17.83, 54.47) * mm, "end": v(18.33, 54.97) * mm});
            skLineSegment(sketch, "E243", {"start": v(18.33, 54.97) * mm, "end": v(18.83, 54.47) * mm});
            skLineSegment(sketch, "E244", {"start": v(18.83, 54.47) * mm, "end": v(20.55, 54.47) * mm});
            skArc(sketch, "E245", {"start": v(20.55, 54.47) * mm, "mid": v(21.5, 54.32) * mm, "end": v(22.34, 53.88) * mm});
            skArc(sketch, "E246", {"start": v(22.34, 53.88) * mm, "mid": v(23.6, 52.08) * mm, "end": v(24.45, 50.04) * mm});
            skArc(sketch, "E247", {"start": v(24.45, 50.04) * mm, "mid": v(24.47, 49.78) * mm, "end": v(24.42, 49.52) * mm});
            skLineSegment(sketch, "E248", {"start": v(24.42, 49.52) * mm, "end": v(23.43, 46.47) * mm});
            skLineSegment(sketch, "E249", {"start": v(23.43, 46.47) * mm, "end": v(21.78, 46.47) * mm});
            skArc(sketch, "E250", {"start": v(21.78, 46.47) * mm, "mid": v(21.57, 46.38) * mm, "end": v(21.48, 46.17) * mm});
            skLineSegment(sketch, "E251", {"start": v(21.48, 46.17) * mm, "end": v(21.48, 44.47) * mm});
            skLineSegment(sketch, "E252", {"start": v(21.48, 44.47) * mm, "end": v(22.28, 43.97) * mm});
            skLineSegment(sketch, "E253", {"start": v(22.28, 43.97) * mm, "end": v(32.33, 43.97) * mm});
            skArc(sketch, "E254", {"start": v(32.33, 43.97) * mm, "mid": v(33.04, 44.26) * mm, "end": v(33.33, 44.97) * mm});
            skLineSegment(sketch, "E255", {"start": v(33.33, 44.97) * mm, "end": v(33.33, 55.02) * mm});
            skLineSegment(sketch, "E256", {"start": v(33.33, 55.02) * mm, "end": v(32.83, 55.82) * mm});
            skLineSegment(sketch, "E257", {"start": v(32.83, 55.82) * mm, "end": v(31.13, 55.82) * mm});
            skArc(sketch, "E258", {"start": v(31.13, 55.82) * mm, "mid": v(30.92, 55.73) * mm, "end": v(30.83, 55.52) * mm});
            skLineSegment(sketch, "E259", {"start": v(30.83, 55.52) * mm, "end": v(30.83, 53.87) * mm});
            skLineSegment(sketch, "E260", {"start": v(30.83, 53.87) * mm, "end": v(27.78, 52.88) * mm});
            skArc(sketch, "E261", {"start": v(27.78, 52.88) * mm, "mid": v(27.52, 52.83) * mm, "end": v(27.26, 52.85) * mm});
            skArc(sketch, "E262", {"start": v(27.26, 52.85) * mm, "mid": v(25.22, 53.7) * mm, "end": v(23.42, 54.96) * mm});
            skArc(sketch, "E263", {"start": v(23.42, 54.96) * mm, "mid": v(22.98, 55.8) * mm, "end": v(22.83, 56.75) * mm});
            skLineSegment(sketch, "E264", {"start": v(22.83, 56.75) * mm, "end": v(22.83, 58.47) * mm});
            skLineSegment(sketch, "E265", {"start": v(22.83, 58.47) * mm, "end": v(22.33, 58.97) * mm});
            skLineSegment(sketch, "E266", {"start": v(22.33, 58.97) * mm, "end": v(22.83, 59.47) * mm});
            skLineSegment(sketch, "E267", {"start": v(22.83, 59.47) * mm, "end": v(22.83, 61.19) * mm});
            skArc(sketch, "E268", {"start": v(22.83, 61.19) * mm, "mid": v(22.98, 62.13) * mm, "end": v(23.42, 62.97) * mm});
            skArc(sketch, "E269", {"start": v(23.42, 62.97) * mm, "mid": v(25.22, 64.24) * mm, "end": v(27.26, 65.08) * mm});
            skArc(sketch, "E270", {"start": v(27.26, 65.08) * mm, "mid": v(27.52, 65.1) * mm, "end": v(27.78, 65.06) * mm});
            skLineSegment(sketch, "E271", {"start": v(27.78, 65.06) * mm, "end": v(30.83, 64.07) * mm});
            skLineSegment(sketch, "E272", {"start": v(30.83, 64.07) * mm, "end": v(30.83, 62.42) * mm});
            skArc(sketch, "E273", {"start": v(30.83, 62.42) * mm, "mid": v(30.92, 62.2) * mm, "end": v(31.13, 62.12) * mm});
            skLineSegment(sketch, "E274", {"start": v(31.13, 62.12) * mm, "end": v(32.83, 62.12) * mm});
            skLineSegment(sketch, "E275", {"start": v(32.83, 62.12) * mm, "end": v(33.33, 62.92) * mm});
            skLineSegment(sketch, "E276", {"start": v(33.33, 62.92) * mm, "end": v(33.33, 72.97) * mm});
            skArc(sketch, "E277", {"start": v(33.33, 72.97) * mm, "mid": v(33.04, 73.68) * mm, "end": v(32.33, 73.97) * mm});
            skLineSegment(sketch, "E278", {"start": v(32.33, 73.97) * mm, "end": v(22.28, 73.97) * mm});
            skLineSegment(sketch, "E279", {"start": v(22.28, 73.97) * mm, "end": v(21.48, 73.47) * mm});
            skLineSegment(sketch, "E280", {"start": v(21.48, 73.47) * mm, "end": v(21.48, 71.77) * mm});
            skArc(sketch, "E281", {"start": v(21.48, 71.77) * mm, "mid": v(21.57, 71.56) * mm, "end": v(21.78, 71.47) * mm});
            skLineSegment(sketch, "E282", {"start": v(21.78, 71.47) * mm, "end": v(23.43, 71.47) * mm});
            skLineSegment(sketch, "E283", {"start": v(23.43, 71.47) * mm, "end": v(24.42, 68.42) * mm});
            skArc(sketch, "E284", {"start": v(24.42, 68.42) * mm, "mid": v(24.47, 68.16) * mm, "end": v(24.45, 67.9) * mm});
            skArc(sketch, "E285", {"start": v(24.45, 67.9) * mm, "mid": v(23.6, 65.86) * mm, "end": v(22.34, 64.06) * mm});
            skArc(sketch, "E286", {"start": v(22.34, 64.06) * mm, "mid": v(21.5, 63.62) * mm, "end": v(20.55, 63.47) * mm});
            skLineSegment(sketch, "E287", {"start": v(20.55, 63.47) * mm, "end": v(18.83, 63.47) * mm});
            skLineSegment(sketch, "E288", {"start": v(18.83, 63.47) * mm, "end": v(18.33, 62.97) * mm});
            skLineSegment(sketch, "E289", {"start": v(18.33, 62.97) * mm, "end": v(17.83, 63.47) * mm});
            skLineSegment(sketch, "E290", {"start": v(17.83, 63.47) * mm, "end": v(16.11, 63.47) * mm});
            skArc(sketch, "E291", {"start": v(16.11, 63.47) * mm, "mid": v(15.17, 63.62) * mm, "end": v(14.33, 64.06) * mm});
            skArc(sketch, "E292", {"start": v(14.33, 64.06) * mm, "mid": v(13.06, 65.86) * mm, "end": v(12.22, 67.9) * mm});
            skArc(sketch, "E293", {"start": v(12.22, 67.9) * mm, "mid": v(12.2, 68.16) * mm, "end": v(12.24, 68.42) * mm});
            skLineSegment(sketch, "E294", {"start": v(12.24, 68.42) * mm, "end": v(13.23, 71.47) * mm});
            skLineSegment(sketch, "E295", {"start": v(13.23, 71.47) * mm, "end": v(14.88, 71.47) * mm});
            skArc(sketch, "E296", {"start": v(14.88, 71.47) * mm, "mid": v(15.1, 71.56) * mm, "end": v(15.18, 71.77) * mm});
            skLineSegment(sketch, "E297", {"start": v(15.18, 71.77) * mm, "end": v(15.18, 73.47) * mm});
            skLineSegment(sketch, "E298", {"start": v(15.18, 73.47) * mm, "end": v(14.38, 73.97) * mm});
            skLineSegment(sketch, "E299", {"start": v(14.38, 73.97) * mm, "end": v(-7.72, 73.97) * mm});
            skLineSegment(sketch, "E300", {"start": v(-7.72, 73.97) * mm, "end": v(-8.52, 73.47) * mm});
            skLineSegment(sketch, "E301", {"start": v(-8.52, 73.47) * mm, "end": v(-8.52, 71.77) * mm});
            skArc(sketch, "E302", {"start": v(-8.52, 71.77) * mm, "mid": v(-8.43, 71.56) * mm, "end": v(-8.22, 71.47) * mm});
            skLineSegment(sketch, "E303", {"start": v(-8.22, 71.47) * mm, "end": v(-6.57, 71.47) * mm});
            skLineSegment(sketch, "E304", {"start": v(-6.57, 71.47) * mm, "end": v(-5.58, 68.42) * mm});
            skArc(sketch, "E305", {"start": v(-5.58, 68.42) * mm, "mid": v(-5.53, 68.16) * mm, "end": v(-5.55, 67.9) * mm});
            skArc(sketch, "E306", {"start": v(-5.55, 67.9) * mm, "mid": v(-6.4, 65.86) * mm, "end": v(-7.66, 64.06) * mm});
            skArc(sketch, "E307", {"start": v(-7.66, 64.06) * mm, "mid": v(-8.5, 63.62) * mm, "end": v(-9.45, 63.47) * mm});
            skLineSegment(sketch, "E308", {"start": v(-9.45, 63.47) * mm, "end": v(-11.17, 63.47) * mm});
            skLineSegment(sketch, "E309", {"start": v(-11.17, 63.47) * mm, "end": v(-11.67, 62.97) * mm});
            skLineSegment(sketch, "E310", {"start": v(-11.67, 62.97) * mm, "end": v(-12.17, 63.47) * mm});
            skLineSegment(sketch, "E311", {"start": v(-12.17, 63.47) * mm, "end": v(-13.89, 63.47) * mm});
            skArc(sketch, "E312", {"start": v(-13.89, 63.47) * mm, "mid": v(-14.83, 63.62) * mm, "end": v(-15.67, 64.06) * mm});
            skArc(sketch, "E313", {"start": v(-15.67, 64.06) * mm, "mid": v(-16.94, 65.86) * mm, "end": v(-17.78, 67.9) * mm});
            skArc(sketch, "E314", {"start": v(-17.78, 67.9) * mm, "mid": v(-17.8, 68.16) * mm, "end": v(-17.76, 68.42) * mm});
            skLineSegment(sketch, "E315", {"start": v(-17.76, 68.42) * mm, "end": v(-16.77, 71.47) * mm});
            skLineSegment(sketch, "E316", {"start": v(-16.77, 71.47) * mm, "end": v(-15.12, 71.47) * mm});
            skArc(sketch, "E317", {"start": v(-15.12, 71.47) * mm, "mid": v(-14.9, 71.56) * mm, "end": v(-14.82, 71.77) * mm});
            skLineSegment(sketch, "E318", {"start": v(-14.82, 71.77) * mm, "end": v(-14.82, 73.47) * mm});
            skLineSegment(sketch, "E319", {"start": v(-14.82, 73.47) * mm, "end": v(-15.62, 73.97) * mm});
            skLineSegment(sketch, "E320", {"start": v(-15.62, 73.97) * mm, "end": v(-25.67, 73.97) * mm});
            skArc(sketch, "E321", {"start": v(-25.67, 73.97) * mm, "mid": v(-26.38, 73.68) * mm, "end": v(-26.67, 72.97) * mm});
            skLineSegment(sketch, "E322", {"start": v(-26.67, 72.97) * mm, "end": v(-26.67, 62.92) * mm});
            skLineSegment(sketch, "E323", {"start": v(-26.67, 62.92) * mm, "end": v(-26.17, 62.12) * mm});
            skLineSegment(sketch, "E324", {"start": v(-26.17, 62.12) * mm, "end": v(-24.47, 62.12) * mm});
            skArc(sketch, "E325", {"start": v(-24.47, 62.12) * mm, "mid": v(-24.26, 62.2) * mm, "end": v(-24.17, 62.42) * mm});
            skLineSegment(sketch, "E326", {"start": v(-24.17, 62.42) * mm, "end": v(-24.17, 64.07) * mm});
            skLineSegment(sketch, "E327", {"start": v(-24.17, 64.07) * mm, "end": v(-21.12, 65.06) * mm});
            skArc(sketch, "E328", {"start": v(-21.12, 65.06) * mm, "mid": v(-20.86, 65.1) * mm, "end": v(-20.6, 65.08) * mm});
            skArc(sketch, "E329", {"start": v(-20.6, 65.08) * mm, "mid": v(-18.56, 64.24) * mm, "end": v(-16.76, 62.97) * mm});
            skArc(sketch, "E330", {"start": v(-16.76, 62.97) * mm, "mid": v(-16.32, 62.13) * mm, "end": v(-16.17, 61.19) * mm});
            skLineSegment(sketch, "E331", {"start": v(-16.17, 61.19) * mm, "end": v(-16.17, 59.47) * mm});
            skLineSegment(sketch, "E332", {"start": v(-16.17, 59.47) * mm, "end": v(-15.67, 58.97) * mm});
            skLineSegment(sketch, "E333", {"start": v(-15.67, 58.97) * mm, "end": v(-16.17, 58.47) * mm});
            skLineSegment(sketch, "E334", {"start": v(-16.17, 58.47) * mm, "end": v(-16.17, 56.75) * mm});
            skArc(sketch, "E335", {"start": v(-16.17, 56.75) * mm, "mid": v(-16.32, 55.8) * mm, "end": v(-16.76, 54.96) * mm});
            skArc(sketch, "E336", {"start": v(-16.76, 54.96) * mm, "mid": v(-18.56, 53.7) * mm, "end": v(-20.6, 52.85) * mm});
            skArc(sketch, "E337", {"start": v(-20.6, 52.85) * mm, "mid": v(-20.86, 52.83) * mm, "end": v(-21.12, 52.88) * mm});
            skLineSegment(sketch, "E338", {"start": v(-21.12, 52.88) * mm, "end": v(-24.17, 53.87) * mm});
            skLineSegment(sketch, "E339", {"start": v(-24.17, 53.87) * mm, "end": v(-24.17, 55.52) * mm});
            skArc(sketch, "E340", {"start": v(-24.17, 55.52) * mm, "mid": v(-24.26, 55.73) * mm, "end": v(-24.47, 55.82) * mm});
            skLineSegment(sketch, "E341", {"start": v(-24.47, 55.82) * mm, "end": v(-26.17, 55.82) * mm});
            skLineSegment(sketch, "E342", {"start": v(-26.17, 55.82) * mm, "end": v(-26.67, 55.02) * mm});
            skLineSegment(sketch, "E343", {"start": v(-26.67, 55.02) * mm, "end": v(-26.67, 44.97) * mm});
            skArc(sketch, "E344", {"start": v(-26.67, 44.97) * mm, "mid": v(-26.38, 44.26) * mm, "end": v(-25.67, 43.97) * mm});
            skLineSegment(sketch, "E345", {"start": v(-25.67, 43.97) * mm, "end": v(-15.62, 43.97) * mm});
            skLineSegment(sketch, "E346", {"start": v(-15.62, 43.97) * mm, "end": v(-14.82, 44.47) * mm});
            skLineSegment(sketch, "E347", {"start": v(-14.82, 44.47) * mm, "end": v(-14.82, 46.17) * mm});
            skArc(sketch, "E348", {"start": v(-14.82, 46.17) * mm, "mid": v(-14.9, 46.38) * mm, "end": v(-15.12, 46.47) * mm});
            skLineSegment(sketch, "E349", {"start": v(-15.12, 46.47) * mm, "end": v(-16.77, 46.47) * mm});
            skLineSegment(sketch, "E350", {"start": v(-16.77, 46.47) * mm, "end": v(-17.76, 49.52) * mm});
            skArc(sketch, "E351", {"start": v(-17.76, 49.52) * mm, "mid": v(-17.8, 49.78) * mm, "end": v(-17.78, 50.04) * mm});
            skArc(sketch, "E352", {"start": v(-17.78, 50.04) * mm, "mid": v(-16.94, 52.08) * mm, "end": v(-15.67, 53.88) * mm});
            skArc(sketch, "E353", {"start": v(-15.67, 53.88) * mm, "mid": v(-14.83, 54.32) * mm, "end": v(-13.89, 54.47) * mm});
            skLineSegment(sketch, "E354", {"start": v(-13.89, 54.47) * mm, "end": v(-12.17, 54.47) * mm});
            skLineSegment(sketch, "E355", {"start": v(-12.17, 54.47) * mm, "end": v(-11.67, 54.97) * mm});
            skLineSegment(sketch, "E356", {"start": v(-11.67, 54.97) * mm, "end": v(-11.17, 54.47) * mm});
            skLineSegment(sketch, "E357", {"start": v(-11.17, 54.47) * mm, "end": v(-9.45, 54.47) * mm});
            skArc(sketch, "E358", {"start": v(-9.45, 54.47) * mm, "mid": v(-8.5, 54.32) * mm, "end": v(-7.66, 53.88) * mm});
            skArc(sketch, "E359", {"start": v(-7.66, 53.88) * mm, "mid": v(-6.4, 52.08) * mm, "end": v(-5.55, 50.04) * mm});
            skArc(sketch, "E360", {"start": v(-5.55, 50.04) * mm, "mid": v(-5.53, 49.78) * mm, "end": v(-5.58, 49.52) * mm});
            skLineSegment(sketch, "E361", {"start": v(-5.58, 49.52) * mm, "end": v(-6.57, 46.47) * mm});
            skLineSegment(sketch, "E362", {"start": v(-6.57, 46.47) * mm, "end": v(-8.22, 46.47) * mm});
            skArc(sketch, "E363", {"start": v(-8.22, 46.47) * mm, "mid": v(-8.43, 46.38) * mm, "end": v(-8.52, 46.17) * mm});
            skLineSegment(sketch, "E364", {"start": v(-8.52, 46.17) * mm, "end": v(-8.52, 44.47) * mm});
            skLineSegment(sketch, "E365", {"start": v(-8.52, 44.47) * mm, "end": v(-7.72, 43.97) * mm});
            skSolve(sketch);
        }
        {
            var Q0;
            Q0=makeQuery(id+"F0.imprint","IMPRINT",FACE,{"disambiguationData":[TD([[makeQuery(id+"F0.imprint","IMPRINT",EDGE,{"derivedFrom":sQuery(id+"F0.wireOp",EDGE,"E0")}),-1.0]])]});
            extrude(context, id + "F1", {"entities" : qUnion([Q0]), "depth" : 320 * mm, "offsetDistance" : 25 * mm});
        }
    });
